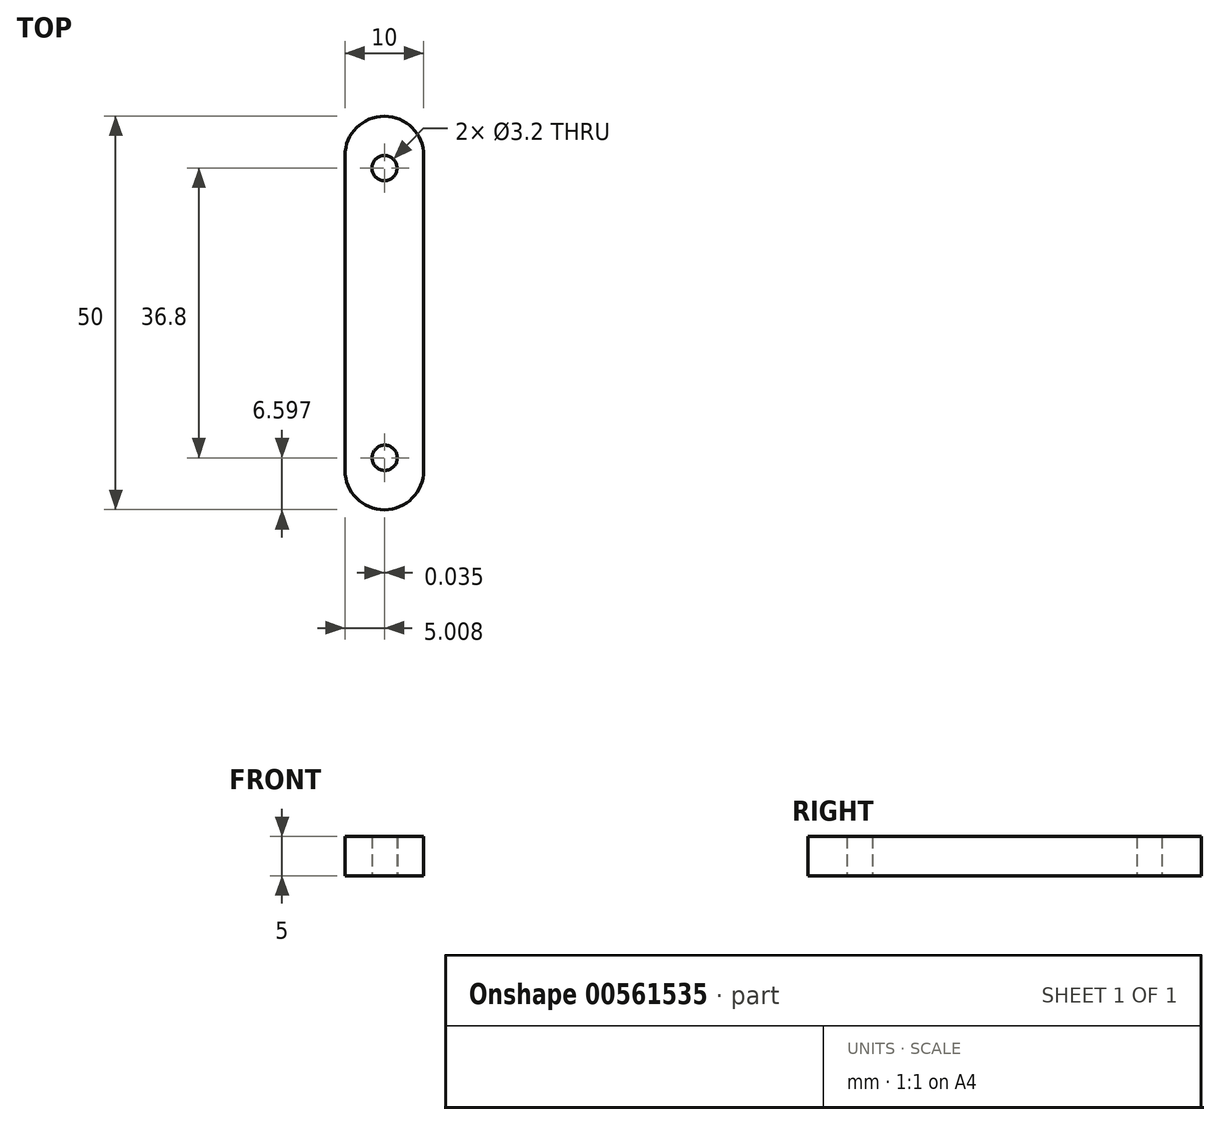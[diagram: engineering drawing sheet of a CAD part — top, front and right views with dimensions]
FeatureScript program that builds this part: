
annotation { "Feature Type Name" : "Feature", "Feature Type Description" : "" }
export const myFeature = defineFeature(function(context is Context, id is Id, definition is map)
    precondition{}
    {
        {
            var Q0;
            Q0=qCreatedBy(makeId("Top.planeOp"),FACE);
            var sketch = newSketch(context, id + "F0", { "sketchPlane" : qUnion([Q0])});
            skLineSegment(sketch, "E0.bottom", {"start": v(2.7, -25.37) * mm, "end": v(-7.3, -25.37) * mm});
            skLineSegment(sketch, "E0.top", {"start": v(2.7, 24.63) * mm, "end": v(-7.3, 24.63) * mm});
            skLineSegment(sketch, "E0.left", {"start": v(2.7, -25.37) * mm, "end": v(2.7, 24.63) * mm});
            skLineSegment(sketch, "E0.right", {"start": v(-7.3, -25.37) * mm, "end": v(-7.3, 24.63) * mm});
            skPoint(sketch, "E0.middle", {"position": v(-2.3, -0.37) * mm});
            skCircle(sketch, "E1", {"center": v(-2.3, 18.03) * mm, "radius": 1.6 * mm});
            skCircle(sketch, "E2", {"center": v(-2.27, -18.77) * mm, "radius": 1.6 * mm});
            skSolve(sketch);
        }
        {
            var Q0;
            Q0=qSketchRegion(id+"F0",true);
            extrude(context, id + "F1", {"entities" : qUnion([Q0]), "depth" : 5 * mm, "offsetDistance" : 25 * mm});
        }
        {
            var Q0;
            Q0=makeQuery(id+"F1.opExtrude","SWEPT_EDGE",EDGE,{"disambiguationData":[OSD([sQuery(id+"F0.wireOp",EDGE,"E0.bottom"),sQuery(id+"F0.wireOp",EDGE,"E0.left")])]});
            var Q1;
            Q1=makeQuery(id+"F1.opExtrude","SWEPT_EDGE",EDGE,{"disambiguationData":[OSD([sQuery(id+"F0.wireOp",EDGE,"E0.bottom"),sQuery(id+"F0.wireOp",EDGE,"E0.right")])]});
            var Q2;
            Q2=makeQuery(id+"F1.opExtrude","SWEPT_EDGE",EDGE,{"disambiguationData":[OSD([sQuery(id+"F0.wireOp",EDGE,"E0.top"),sQuery(id+"F0.wireOp",EDGE,"E0.left")])]});
            var Q3;
            Q3=makeQuery(id+"F1.opExtrude","SWEPT_EDGE",EDGE,{"disambiguationData":[OSD([sQuery(id+"F0.wireOp",EDGE,"E0.top"),sQuery(id+"F0.wireOp",EDGE,"E0.right")])]});
            fillet(context, id + "F2", {"entities" : qUnion([Q0, Q1, Q2, Q3]), "radius" : 5 * mm, "tangentPropagation" : true, "allowEdgeOverflow" : false});
        }
    });
